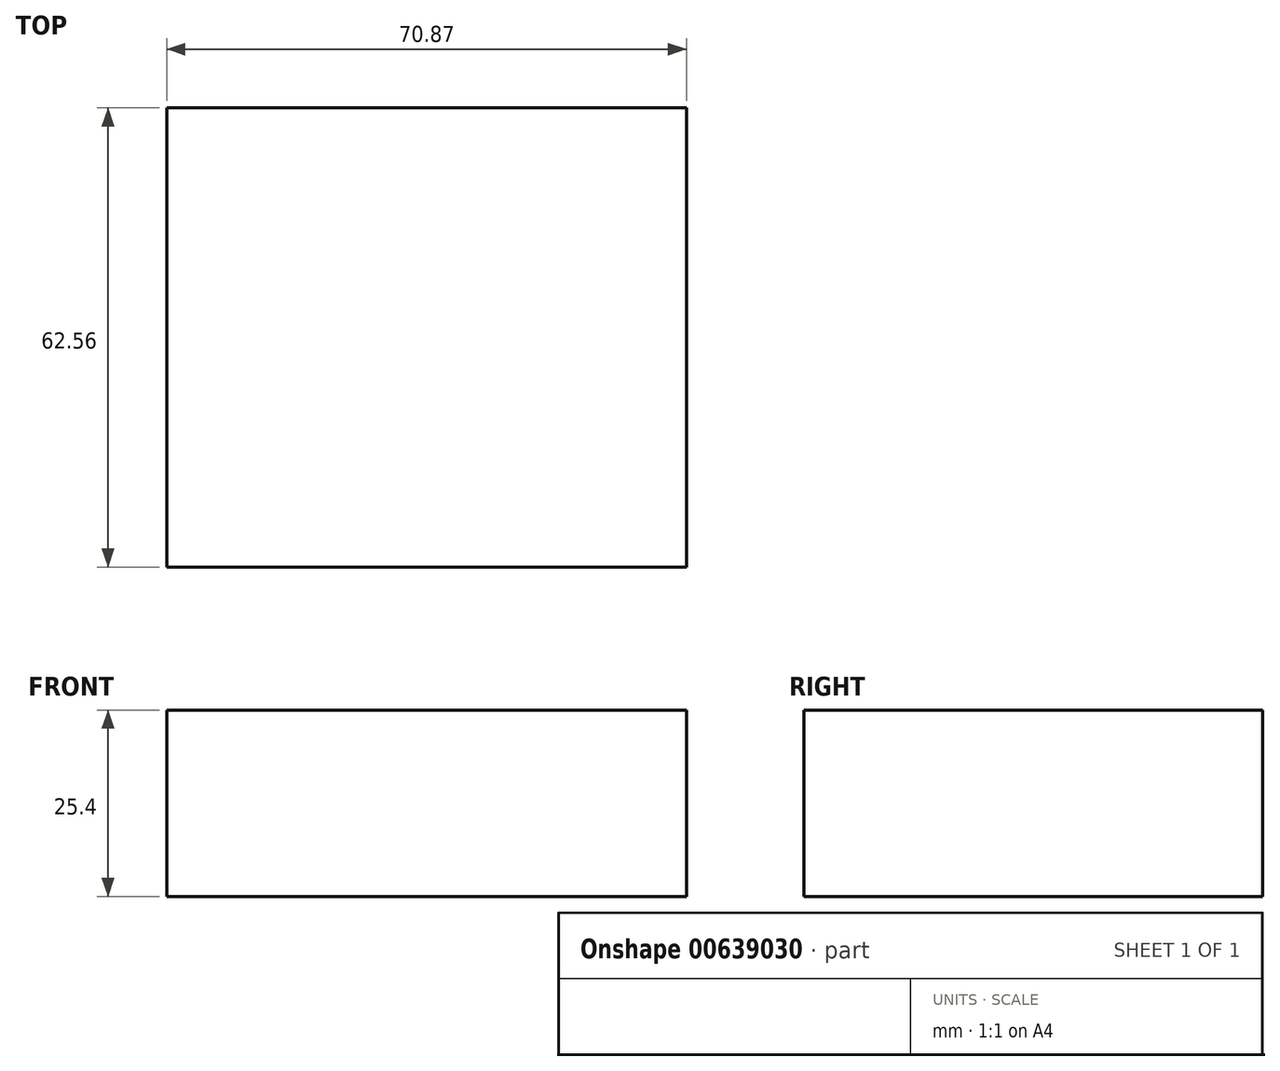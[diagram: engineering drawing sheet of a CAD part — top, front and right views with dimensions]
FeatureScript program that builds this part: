
annotation { "Feature Type Name" : "Feature", "Feature Type Description" : "" }
export const myFeature = defineFeature(function(context is Context, id is Id, definition is map)
    precondition{}
    {
        {
            var Q0;
            Q0=qCreatedBy(makeId("Top.planeOp"),FACE);
            var sketch = newSketch(context, id + "F0", { "sketchPlane" : qUnion([Q0])});
            skLineSegment(sketch, "E0.bottom", {"start": v(0, 0) * mm, "end": v(-70.87, 0) * mm});
            skLineSegment(sketch, "E0.top", {"start": v(0, 62.56) * mm, "end": v(-70.87, 62.56) * mm});
            skLineSegment(sketch, "E0.left", {"start": v(0, 0) * mm, "end": v(0, 62.56) * mm});
            skLineSegment(sketch, "E0.right", {"start": v(-70.87, 0) * mm, "end": v(-70.87, 62.56) * mm});
            skSolve(sketch);
        }
        {
            var Q0;
            Q0=makeQuery(id+"F0.imprint","IMPRINT",FACE,{"disambiguationData":[TD([[makeQuery(id+"F0.imprint","IMPRINT",EDGE,{"derivedFrom":sQuery(id+"F0.wireOp",EDGE,"E0.bottom")}),-1.0]])]});
            var Q1;
            Q1=sQuery(id+"F0.wireOp",EDGE,"E0.left");
            var Q2;
            Q2=sQuery(id+"F0.wireOp",EDGE,"E0.bottom");
            var Q3;
            Q3=sQuery(id+"F0.wireOp",EDGE,"E0.right");
            var Q4;
            Q4=sQuery(id+"F0.wireOp",EDGE,"E0.top");
            extrude(context, id + "F1", {"entities" : qUnion([Q0]), "bodyType" : ToolBodyType.SURFACE, "operationType" : NewBodyOperationType.INTERSECT, "surfaceEntities" : qUnion([Q1, Q2, Q3, Q4]), "depth" : 25.4 * mm, "offsetDistance" : 25.4 * mm});
        }
    });
